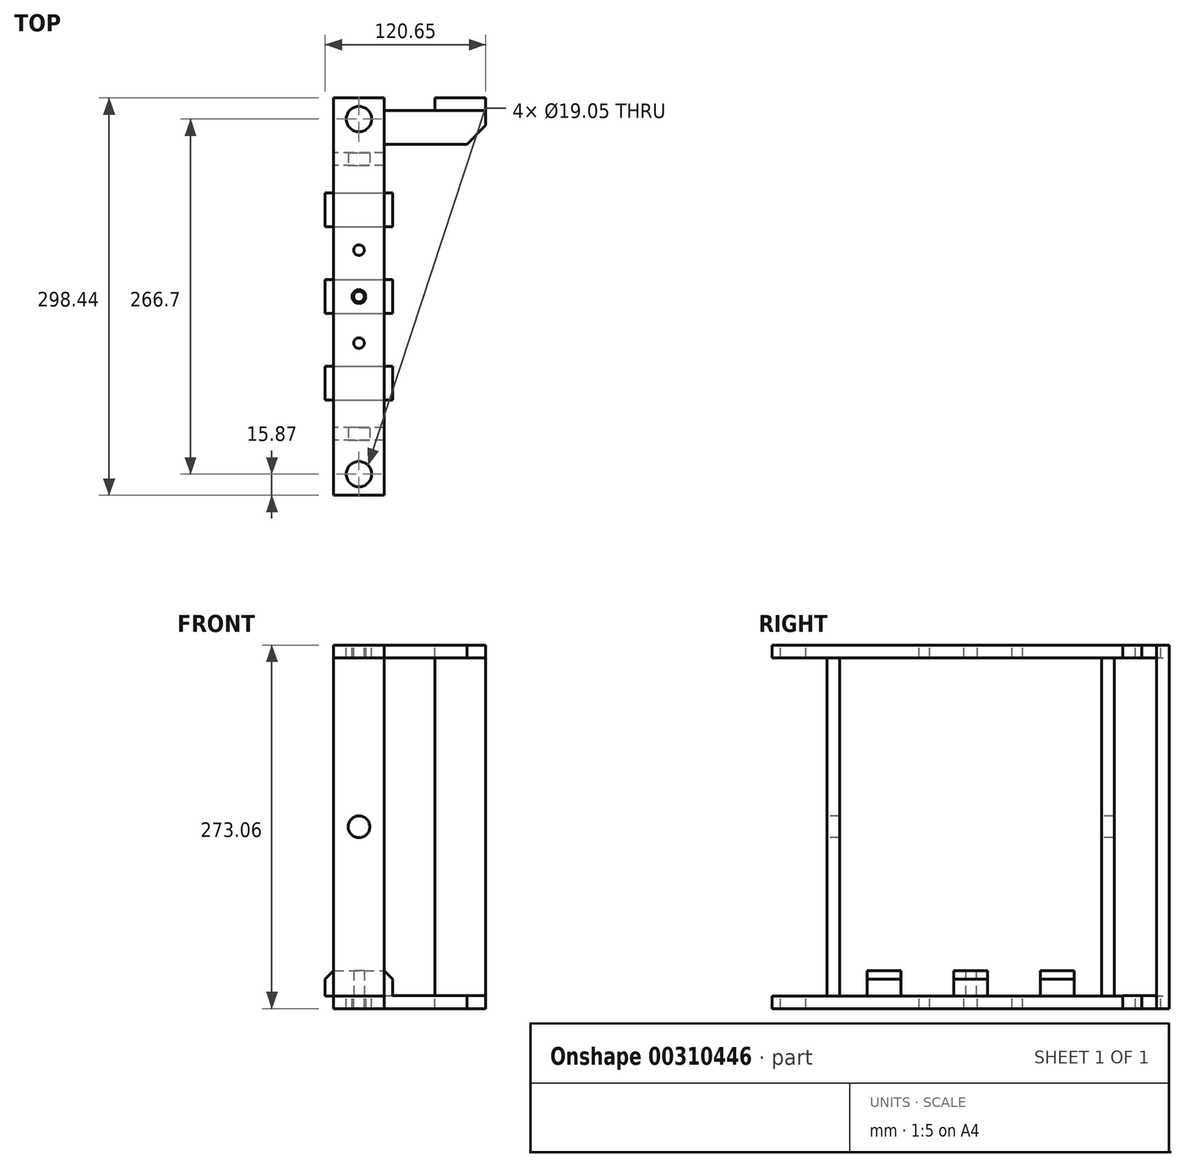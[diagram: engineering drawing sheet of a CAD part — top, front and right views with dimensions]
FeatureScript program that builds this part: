
annotation { "Feature Type Name" : "Feature", "Feature Type Description" : "" }
export const myFeature = defineFeature(function(context is Context, id is Id, definition is map)
    precondition{}
    {
        {
            var Q0;
            Q0=qCreatedBy(makeId("Right.planeOp"),FACE);
            var sketch = newSketch(context, id + "F0", { "sketchPlane" : qUnion([Q0])});
            skLineSegment(sketch, "E0.bottom", {"start": v(-149.22, 136.53) * mm, "end": v(149.23, 136.53) * mm, "construction": true});
            skLineSegment(sketch, "E0.top", {"start": v(-149.23, -136.53) * mm, "end": v(149.22, -136.53) * mm, "construction": true});
            skLineSegment(sketch, "E0.left", {"start": v(-149.22, 136.53) * mm, "end": v(-149.23, -136.53) * mm, "construction": true});
            skLineSegment(sketch, "E0.right", {"start": v(149.23, 136.53) * mm, "end": v(149.22, -136.53) * mm, "construction": true});
            skPoint(sketch, "E0.middle", {"position": v(0, 0) * mm});
            skLineSegment(sketch, "E1", {"start": v(-256.39, 0) * mm, "end": v(244.4, 0) * mm, "construction": true});
            skLineSegment(sketch, "E2", {"start": v(0, 223.18) * mm, "end": v(0, -206.77) * mm, "construction": true});
            skLineSegment(sketch, "E3.bottom", {"start": v(-149.22, 136.53) * mm, "end": v(149.22, 136.53) * mm});
            skLineSegment(sketch, "E3.top", {"start": v(-149.23, 127) * mm, "end": v(149.22, 127) * mm});
            skLineSegment(sketch, "E3.left", {"start": v(-149.22, 136.53) * mm, "end": v(-149.22, 127) * mm});
            skLineSegment(sketch, "E3.right", {"start": v(149.23, 136.53) * mm, "end": v(149.23, 127) * mm});
            skLineSegment(sketch, "E4.MirrorCS", {"start": v(149.23, -136.53) * mm, "end": v(149.23, -127) * mm});
            skLineSegment(sketch, "E5.MirrorCS", {"start": v(-149.22, -136.53) * mm, "end": v(-149.22, -127) * mm});
            skLineSegment(sketch, "E6.MirrorCS", {"start": v(-149.22, -136.53) * mm, "end": v(149.23, -136.53) * mm, "construction": true});
            skLineSegment(sketch, "E7.MirrorCS", {"start": v(-149.22, -136.53) * mm, "end": v(149.22, -136.53) * mm});
            skLineSegment(sketch, "E8.MirrorCS", {"start": v(-149.23, -127) * mm, "end": v(149.22, -127) * mm});
            skSolve(sketch);
        }
        {
            var Q0;
            Q0 = qSketchRegion(id + "F0", true);
            extrude(context, id + "F1", {"entities" : qUnion([Q0]), "endBound" : BoundingType.SYMMETRIC, "depth" : 38.1 * mm});
        }
        {
            var Q0;
            Q0=qCreatedBy(makeId("Right.planeOp"),FACE);
            var sketch = newSketch(context, id + "F2", { "sketchPlane" : qUnion([Q0])});
            skLineSegment(sketch, "E9.0", {"start": v(-98.43, 223.18) * mm, "end": v(-98.43, -206.77) * mm, "construction": true});
            skLineSegment(sketch, "E10.0", {"start": v(-149.23, 127) * mm, "end": v(149.22, 127) * mm, "construction": true});
            skLineSegment(sketch, "E11.0", {"start": v(-149.23, -127) * mm, "end": v(149.22, -127) * mm, "construction": true});
            skLineSegment(sketch, "E12.bottom", {"start": v(-98.43, 127) * mm, "end": v(-107.95, 127) * mm});
            skLineSegment(sketch, "E12.top", {"start": v(-98.43, -127) * mm, "end": v(-107.95, -127) * mm});
            skLineSegment(sketch, "E12.left", {"start": v(-98.43, 127) * mm, "end": v(-98.43, -127) * mm});
            skLineSegment(sketch, "E12.right", {"start": v(-107.95, 127) * mm, "end": v(-107.95, -127) * mm});
            skLineSegment(sketch, "E13.MirrorCS", {"start": v(98.43, 127) * mm, "end": v(107.95, 127) * mm});
            skLineSegment(sketch, "E14.MirrorCS", {"start": v(98.43, -127) * mm, "end": v(107.95, -127) * mm});
            skLineSegment(sketch, "E15.MirrorCS", {"start": v(98.43, 127) * mm, "end": v(98.43, -127) * mm});
            skLineSegment(sketch, "E16.MirrorCS", {"start": v(107.95, 127) * mm, "end": v(107.95, -127) * mm});
            skSolve(sketch);
        }
        {
            var Q0;
            Q0 = qSketchRegion(id + "F2", true);
            extrude(context, id + "F3", {"entities" : qUnion([Q0]), "endBound" : BoundingType.SYMMETRIC, "depth" : 38.1 * mm});
        }
        {
            var Q0;
            Q0=makeQuery(id+"F1.opExtrude","SWEPT_FACE",FACE,{"disambiguationData":[OSD([sQuery(id+"F0.wireOp",EDGE,"E3.bottom")])]});
            var sketch = newSketch(context, id + "F4", { "sketchPlane" : qUnion([Q0])});
            skLineSegment(sketch, "E17", {"start": v(-116.2, 0) * mm, "end": v(100.71, 0) * mm, "construction": true});
            skLineSegment(sketch, "E18.0", {"start": v(0, -256.39) * mm, "end": v(0, 244.4) * mm, "construction": true});
            skLineSegment(sketch, "E19.0", {"start": v(-116.2, -133.35) * mm, "end": v(100.71, -133.35) * mm, "construction": true});
            skPoint(sketch, "E20", {"position": v(0, -133.35) * mm});
            skPoint(sketch, "E21.MirrorP", {"position": v(0, 133.35) * mm});
            skSolve(sketch);
        }
        {
            var Q0;
            Q0=sQuery(id+"F4.wireOp",VERTEX,"E20");
            var Q1;
            Q1=sQuery(id+"F4.wireOp",VERTEX,"E21.MirrorP");
            var Q2;
            Q2=makeQuery(id+"F1.opExtrude","SWEPT_BODY",BODY,{"disambiguationData":[OSD([sQuery(id+"F0.wireOp",EDGE,"E3.bottom"),sQuery(id+"F0.wireOp",EDGE,"E3.top"),sQuery(id+"F0.wireOp",EDGE,"E3.left"),sQuery(id+"F0.wireOp",EDGE,"E3.right")])]});
            var Q3;
            Q3=makeQuery(id+"F1.opExtrude","SWEPT_BODY",BODY,{"disambiguationData":[OSD([sQuery(id+"F0.wireOp",EDGE,"E4.MirrorCS"),sQuery(id+"F0.wireOp",EDGE,"E5.MirrorCS"),sQuery(id+"F0.wireOp",EDGE,"E7.MirrorCS"),sQuery(id+"F0.wireOp",EDGE,"E8.MirrorCS")])]});
            hole(context, id + "F5", {"style" : HoleStyle.SIMPLE, "endStyle" : HoleEndStyle.THROUGH, "holeDiameter" : 19.05 * mm, "tappedDepth" : 24.13 * mm, "tapClearance" : 3, "startFromSketch" : true, "locations" : qUnion([Q0, Q1]), "scope" : qUnion([Q2, Q3])});
        }
        {
            var Q0;
            Q0=makeQuery(id+"F1.opExtrude","SWEPT_FACE",FACE,{"disambiguationData":[OSD([sQuery(id+"F0.wireOp",EDGE,"E3.bottom")])]});
            var sketch = newSketch(context, id + "F6", { "sketchPlane" : qUnion([Q0])});
            skLineSegment(sketch, "E22.0", {"start": v(0, -256.39) * mm, "end": v(0, 244.4) * mm, "construction": true});
            skLineSegment(sketch, "E23", {"start": v(-103.62, 0) * mm, "end": v(109.91, 0) * mm, "construction": true});
            skLineSegment(sketch, "E24.0", {"start": v(-103.62, -34.93) * mm, "end": v(109.91, -34.92) * mm, "construction": true});
            skPoint(sketch, "E25", {"position": v(0, -34.93) * mm});
            skPoint(sketch, "E26", {"position": v(0, 0) * mm});
            skPoint(sketch, "E27.MirrorP", {"position": v(0, 34.93) * mm});
            skSolve(sketch);
        }
        {
            var Q0;
            Q0=sQuery(id+"F6.wireOp",VERTEX,"E25");
            var Q1;
            Q1=sQuery(id+"F6.wireOp",VERTEX,"E27.MirrorP");
            var Q2;
            Q2=makeQuery(id+"F1.opExtrude","SWEPT_BODY",BODY,{"disambiguationData":[OSD([sQuery(id+"F0.wireOp",EDGE,"E3.bottom"),sQuery(id+"F0.wireOp",EDGE,"E3.top"),sQuery(id+"F0.wireOp",EDGE,"E3.left"),sQuery(id+"F0.wireOp",EDGE,"E3.right")])]});
            var Q3;
            Q3=makeQuery(id+"F1.opExtrude","SWEPT_BODY",BODY,{"disambiguationData":[OSD([sQuery(id+"F0.wireOp",EDGE,"E4.MirrorCS"),sQuery(id+"F0.wireOp",EDGE,"E5.MirrorCS"),sQuery(id+"F0.wireOp",EDGE,"E7.MirrorCS"),sQuery(id+"F0.wireOp",EDGE,"E8.MirrorCS")])]});
            hole(context, id + "F7", {"style" : HoleStyle.SIMPLE, "endStyle" : HoleEndStyle.THROUGH, "standardTappedOrClearance" : lookupTablePath({ "standard" : "ANSI", "engagement" : "75%", "pitch" : "16 tpi", "size" : "3/8", "type" : "Tapped" }), "standardBlindInLast" : lookupTablePath({ "standard" : "ANSI", "engagement" : "75%", "pitch" : "16 tpi", "size" : "3/8", "type" : "Tapped" }), "holeDiameter" : 7.94 * mm, "showTappedDepth" : true, "tappedDepth" : 24.13 * mm, "tapClearance" : 3, "startFromSketch" : true, "locations" : qUnion([Q0, Q1]), "scope" : qUnion([Q2, Q3]), "majorDiameter" : 9.53 * mm});
        }
        {
            var Q0;
            Q0=sQuery(id+"F6.wireOp",VERTEX,"E26");
            var Q1;
            Q1=makeQuery(id+"F1.opExtrude","SWEPT_BODY",BODY,{"disambiguationData":[OSD([sQuery(id+"F0.wireOp",EDGE,"E3.bottom"),sQuery(id+"F0.wireOp",EDGE,"E3.top"),sQuery(id+"F0.wireOp",EDGE,"E3.left"),sQuery(id+"F0.wireOp",EDGE,"E3.right")])]});
            var Q2;
            Q2=makeQuery(id+"F1.opExtrude","SWEPT_BODY",BODY,{"disambiguationData":[OSD([sQuery(id+"F0.wireOp",EDGE,"E4.MirrorCS"),sQuery(id+"F0.wireOp",EDGE,"E5.MirrorCS"),sQuery(id+"F0.wireOp",EDGE,"E7.MirrorCS"),sQuery(id+"F0.wireOp",EDGE,"E8.MirrorCS")])]});
            hole(context, id + "F8", {"style" : HoleStyle.SIMPLE, "endStyle" : HoleEndStyle.THROUGH, "holeDiameter" : 10.3 * mm, "tappedDepth" : 24.13 * mm, "tapClearance" : 3, "startFromSketch" : true, "locations" : qUnion([Q0]), "scope" : qUnion([Q1, Q2])});
        }
        {
            var Q0;
            Q0=makeQuery(id+"F3.opExtrude","SWEPT_FACE",FACE,{"disambiguationData":[OSD([sQuery(id+"F2.wireOp",EDGE,"E12.right")])]});
            var sketch = newSketch(context, id + "F9", { "sketchPlane" : qUnion([Q0])});
            skLineSegment(sketch, "E28.0", {"start": v(19.05, -127) * mm, "end": v(-19.05, -127) * mm, "construction": true});
            skLineSegment(sketch, "E29.0", {"start": v(19.05, 0) * mm, "end": v(-19.05, 0) * mm, "construction": true});
            skPoint(sketch, "E30", {"position": v(0, 0) * mm});
            skSolve(sketch);
        }
        {
            var Q0;
            Q0=sQuery(id+"F9.wireOp",VERTEX,"E30");
            var Q1;
            Q1=makeQuery(id+"F3.opExtrude","SWEPT_BODY",BODY,{"disambiguationData":[OSD([sQuery(id+"F2.wireOp",EDGE,"E12.bottom"),sQuery(id+"F2.wireOp",EDGE,"E12.top"),sQuery(id+"F2.wireOp",EDGE,"E12.left"),sQuery(id+"F2.wireOp",EDGE,"E12.right")])]});
            var Q2;
            Q2=makeQuery(id+"F3.opExtrude","SWEPT_BODY",BODY,{"disambiguationData":[OSD([sQuery(id+"F2.wireOp",EDGE,"E13.MirrorCS"),sQuery(id+"F2.wireOp",EDGE,"E14.MirrorCS"),sQuery(id+"F2.wireOp",EDGE,"E15.MirrorCS"),sQuery(id+"F2.wireOp",EDGE,"E16.MirrorCS")])]});
            hole(context, id + "F10", {"style" : HoleStyle.SIMPLE, "endStyle" : HoleEndStyle.THROUGH, "holeDiameter" : 16.26 * mm, "tappedDepth" : 24.13 * mm, "tapClearance" : 3, "startFromSketch" : true, "locations" : qUnion([Q0]), "scope" : qUnion([Q1, Q2])});
        }
        {
            var Q0;
            Q0=makeQuery(id+"F1.opExtrude","SWEPT_FACE",FACE,{"disambiguationData":[OSD([sQuery(id+"F0.wireOp",EDGE,"E8.MirrorCS")])]});
            var sketch = newSketch(context, id + "F11", { "sketchPlane" : qUnion([Q0])});
            skLineSegment(sketch, "E31.bottom", {"start": v(-25.4, -12.7) * mm, "end": v(25.4, -12.7) * mm});
            skLineSegment(sketch, "E31.top", {"start": v(-25.4, 12.7) * mm, "end": v(25.4, 12.7) * mm});
            skLineSegment(sketch, "E31.left", {"start": v(-25.4, -12.7) * mm, "end": v(-25.4, 12.7) * mm});
            skLineSegment(sketch, "E31.right", {"start": v(25.4, -12.7) * mm, "end": v(25.4, 12.7) * mm});
            skPoint(sketch, "E31.middle", {"position": v(0, 0) * mm});
            skLineSegment(sketch, "E32.0.1.0", {"start": v(-25.4, 52.32) * mm, "end": v(25.4, 52.32) * mm});
            skLineSegment(sketch, "E32.0.1.1", {"start": v(-25.4, 77.72) * mm, "end": v(25.4, 77.72) * mm});
            skLineSegment(sketch, "E32.0.1.2", {"start": v(-25.4, 52.32) * mm, "end": v(-25.4, 77.72) * mm});
            skLineSegment(sketch, "E32.0.1.3", {"start": v(25.4, 52.32) * mm, "end": v(25.4, 77.72) * mm});
            skPoint(sketch, "E32.0.1.4", {"position": v(0, 65.02) * mm});
            skLineSegment(sketch, "E32.direction1", {"start": v(-25.4, -12.7) * mm, "end": v(0, -12.7) * mm, "construction": true});
            skLineSegment(sketch, "E32.direction2", {"start": v(-25.4, -12.7) * mm, "end": v(-25.4, 52.32) * mm, "construction": true});
            skLineSegment(sketch, "E33.0.1.0", {"start": v(-25.4, -77.72) * mm, "end": v(25.4, -77.72) * mm});
            skLineSegment(sketch, "E33.0.1.1", {"start": v(25.4, -77.72) * mm, "end": v(25.4, -52.32) * mm});
            skLineSegment(sketch, "E33.0.1.2", {"start": v(-25.4, -77.72) * mm, "end": v(-25.4, -52.32) * mm});
            skLineSegment(sketch, "E33.0.1.3", {"start": v(-25.4, -52.32) * mm, "end": v(25.4, -52.32) * mm});
            skLineSegment(sketch, "E33.0.1.4", {"start": v(-25.4, -77.72) * mm, "end": v(0, -77.72) * mm, "construction": true});
            skPoint(sketch, "E33.0.1.5", {"position": v(0, -65.02) * mm});
            skLineSegment(sketch, "E33.direction2", {"start": v(-25.4, -12.7) * mm, "end": v(-25.4, -77.72) * mm, "construction": true});
            skSolve(sketch);
        }
        {
            var Q0;
            Q0 = qSketchRegion(id + "F11", true);
            extrude(context, id + "F12", {"entities" : qUnion([Q0]), "depth" : 19.05 * mm});
        }
        {
            var Q0;
            Q0=makeQuery(id+"F12.opExtrude","CAP_EDGE",EDGE,{"disambiguationData":[OSD([sQuery(id+"F11.wireOp",EDGE,"E33.0.1.1")])],"isStart":false});
            var Q1;
            Q1=makeQuery(id+"F12.opExtrude","CAP_EDGE",EDGE,{"disambiguationData":[OSD([sQuery(id+"F11.wireOp",EDGE,"E33.0.1.2")])],"isStart":false});
            var Q2;
            Q2=makeQuery(id+"F12.opExtrude","CAP_EDGE",EDGE,{"disambiguationData":[OSD([sQuery(id+"F11.wireOp",EDGE,"E31.left")])],"isStart":false});
            var Q3;
            Q3=makeQuery(id+"F12.opExtrude","CAP_EDGE",EDGE,{"disambiguationData":[OSD([sQuery(id+"F11.wireOp",EDGE,"E31.right")])],"isStart":false});
            var Q4;
            Q4=makeQuery(id+"F12.opExtrude","CAP_EDGE",EDGE,{"disambiguationData":[OSD([sQuery(id+"F11.wireOp",EDGE,"E32.0.1.3")])],"isStart":false});
            var Q5;
            Q5=makeQuery(id+"F12.opExtrude","CAP_EDGE",EDGE,{"disambiguationData":[OSD([sQuery(id+"F11.wireOp",EDGE,"E32.0.1.2")])],"isStart":false});
            chamfer(context, id + "F13", {"entities" : qUnion([Q0, Q1, Q2, Q3, Q4, Q5]), "width" : 6.35 * mm, "tangentPropagation" : true});
        }
        {
            var Q0;
            Q0=makeQuery(id+"F1.opExtrude","SWEPT_FACE",FACE,{"disambiguationData":[OSD([sQuery(id+"F0.wireOp",EDGE,"E3.bottom")])]});
            var sketch = newSketch(context, id + "F14", { "sketchPlane" : qUnion([Q0])});
            skLineSegment(sketch, "E34.0", {"start": v(163.96, 149.22) * mm, "end": v(-19.05, 149.22) * mm, "construction": true});
            skPoint(sketch, "E35.orphan", {"position": v(19.05, 149.22) * mm});
            skLineSegment(sketch, "E36.0", {"start": v(19.05, -149.22) * mm, "end": v(19.05, 149.22) * mm, "construction": true});
            skLineSegment(sketch, "E37.0", {"start": v(163.96, 139.7) * mm, "end": v(-19.05, 139.7) * mm, "construction": true});
            skLineSegment(sketch, "E38.bottom", {"start": v(19.05, 139.7) * mm, "end": v(95.25, 139.7) * mm});
            skLineSegment(sketch, "E38.top", {"start": v(19.05, 114.3) * mm, "end": v(95.25, 114.3) * mm});
            skLineSegment(sketch, "E38.left", {"start": v(19.05, 139.7) * mm, "end": v(19.05, 114.3) * mm});
            skLineSegment(sketch, "E38.right", {"start": v(95.25, 139.7) * mm, "end": v(95.25, 114.3) * mm});
            skSolve(sketch);
        }
        {
            var Q0;
            Q0 = qSketchRegion(id + "F14", true);
            extrude(context, id + "F15", {"entities" : qUnion([Q0]), "oppositeDirection" : true, "depth" : 9.65 * mm});
        }
        {
            var Q0;
            Q0=makeQuery(id+"F15.opExtrude","SWEPT_EDGE",EDGE,{"disambiguationData":[OSD([sQuery(id+"F14.wireOp",EDGE,"E38.top"),sQuery(id+"F14.wireOp",EDGE,"E38.right")])]});
            chamfer(context, id + "F16", {"entities" : qUnion([Q0]), "width" : 14.22 * mm, "tangentPropagation" : true});
        }
        {
            var Q0;
            Q0=makeQuery(id+"F15.opExtrude","SWEPT_BODY",BODY,{"disambiguationData":[OSD([sQuery(id+"F14.wireOp",EDGE,"E38.bottom"),sQuery(id+"F14.wireOp",EDGE,"E38.top"),sQuery(id+"F14.wireOp",EDGE,"E38.left"),sQuery(id+"F14.wireOp",EDGE,"E38.right")])]});
            var Q1;
            Q1=qCreatedBy(makeId("Top.planeOp"),FACE);
            mirror(context, id + "F17", {"entities" : qUnion([Q0]), "mirrorPlane" : qUnion([Q1])});
        }
        {
            var Q0;
            Q0=makeQuery(id+"F15.opExtrude","CAP_FACE",FACE,{"disambiguationData":[OSD([sQuery(id+"F14.wireOp",EDGE,"E38.bottom"),sQuery(id+"F14.wireOp",EDGE,"E38.top"),sQuery(id+"F14.wireOp",EDGE,"E38.left"),sQuery(id+"F14.wireOp",EDGE,"E38.right")])],"isStart":true});
            var sketch = newSketch(context, id + "F18", { "sketchPlane" : qUnion([Q0])});
            skLineSegment(sketch, "E39.0", {"start": v(19.05, 139.7) * mm, "end": v(95.25, 139.7) * mm, "construction": true});
            skLineSegment(sketch, "E40.bottom", {"start": v(95.25, 139.7) * mm, "end": v(57.15, 139.7) * mm});
            skLineSegment(sketch, "E40.top", {"start": v(95.25, 149.22) * mm, "end": v(57.15, 149.22) * mm});
            skLineSegment(sketch, "E40.left", {"start": v(95.25, 139.7) * mm, "end": v(95.25, 149.22) * mm});
            skLineSegment(sketch, "E40.right", {"start": v(57.15, 139.7) * mm, "end": v(57.15, 149.22) * mm});
            skSolve(sketch);
        }
        {
            var Q0;
            Q0 = qSketchRegion(id + "F18", true);
            extrude(context, id + "F19", {"entities" : qUnion([Q0]), "oppositeDirection" : true, "depth" : 273.05 * mm});
        }
        {
            var Q0;
            Q0=makeQuery(id+"F12.opExtrude","CAP_FACE",FACE,{"disambiguationData":[OSD([sQuery(id+"F11.wireOp",EDGE,"E31.bottom"),sQuery(id+"F11.wireOp",EDGE,"E31.top"),sQuery(id+"F11.wireOp",EDGE,"E31.left"),sQuery(id+"F11.wireOp",EDGE,"E31.right")])],"isStart":true});
            var sketch = newSketch(context, id + "F20", { "sketchPlane" : qUnion([Q0])});
            skCircle(sketch, "E41.0", {"center": v(0, 0) * mm, "radius": 5.16 * mm, "construction": true});
            skSolve(sketch);
        }
        {
            var Q0;
            Q0=sQuery(id+"F20.wireOp",VERTEX,"E41.0.center");
            var Q1;
            Q1=makeQuery(id+"F12.opExtrude","SWEPT_BODY",BODY,{"disambiguationData":[OSD([sQuery(id+"F11.wireOp",EDGE,"E31.bottom"),sQuery(id+"F11.wireOp",EDGE,"E31.top"),sQuery(id+"F11.wireOp",EDGE,"E31.left"),sQuery(id+"F11.wireOp",EDGE,"E31.right")])]});
            hole(context, id + "F21", {"style" : HoleStyle.SIMPLE, "endStyle" : HoleEndStyle.THROUGH, "standardTappedOrClearance" : lookupTablePath({ "standard" : "ANSI", "engagement" : "75%", "pitch" : "16 tpi", "size" : "3/8", "type" : "Tapped" }), "standardBlindInLast" : lookupTablePath({ "standard" : "ANSI", "engagement" : "75%", "pitch" : "16 tpi", "size" : "3/8", "type" : "Tapped" }), "holeDiameter" : 7.94 * mm, "showTappedDepth" : true, "tappedDepth" : 24.13 * mm, "tapClearance" : 3, "startFromSketch" : true, "locations" : qUnion([Q0]), "scope" : qUnion([Q1]), "majorDiameter" : 9.53 * mm});
        }
    });
